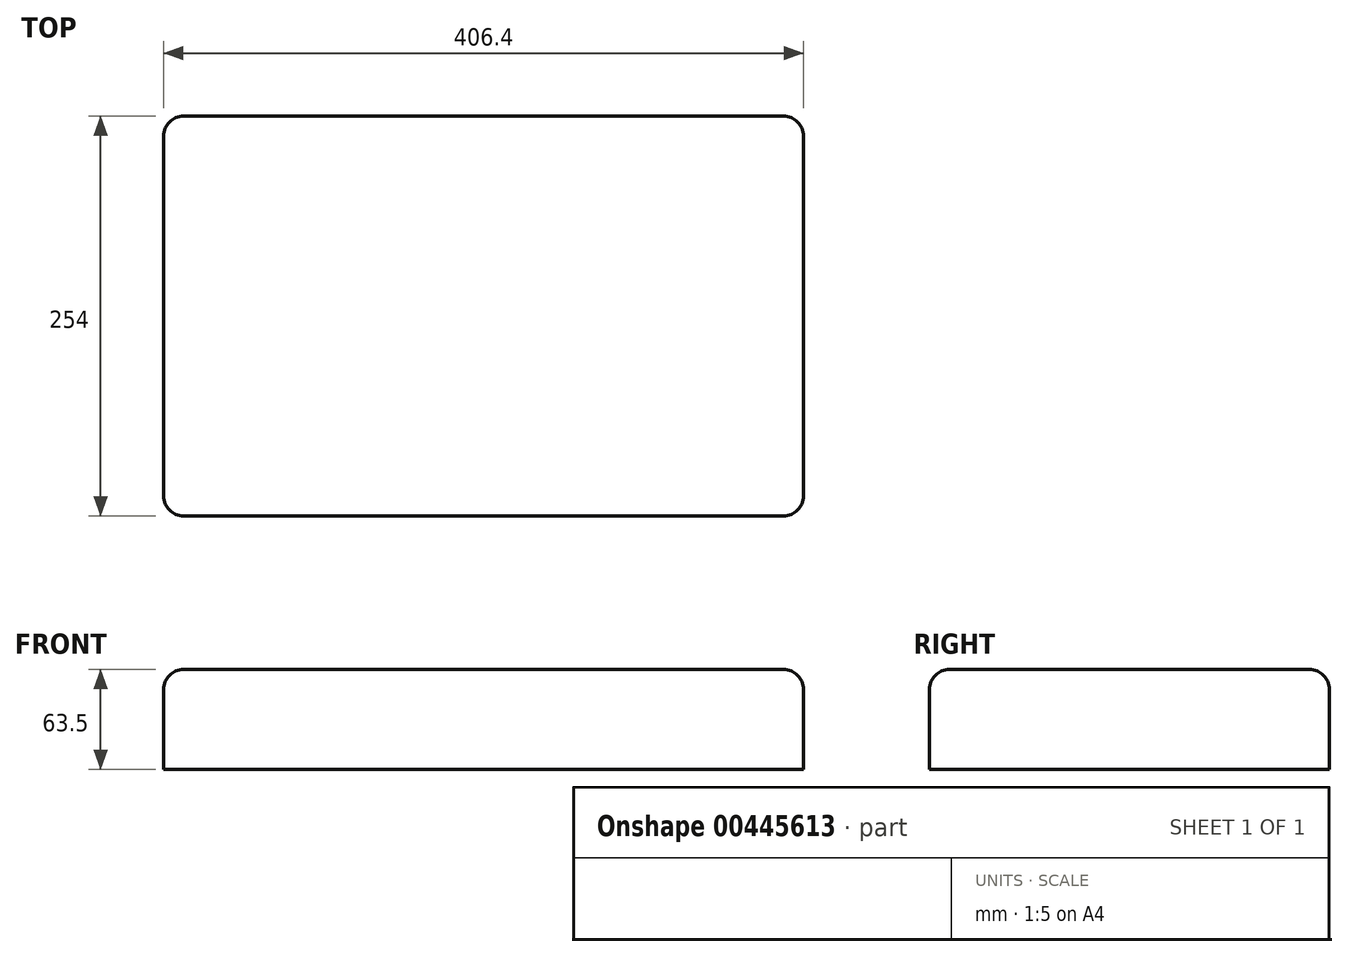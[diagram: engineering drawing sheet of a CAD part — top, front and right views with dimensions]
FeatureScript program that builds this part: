
annotation { "Feature Type Name" : "Feature", "Feature Type Description" : "" }
export const myFeature = defineFeature(function(context is Context, id is Id, definition is map)
    precondition{}
    {
        {
            var Q0;
            Q0=qCreatedBy(makeId("Top.planeOp"),FACE);
            var sketch = newSketch(context, id + "F0", { "sketchPlane" : qUnion([Q0])});
            skLineSegment(sketch, "E0.bottom", {"start": v(203.2, 127) * mm, "end": v(-203.2, 127) * mm});
            skLineSegment(sketch, "E0.top", {"start": v(203.2, -127) * mm, "end": v(-203.2, -127) * mm});
            skLineSegment(sketch, "E0.left", {"start": v(203.2, 127) * mm, "end": v(203.2, -127) * mm});
            skLineSegment(sketch, "E0.right", {"start": v(-203.2, 127) * mm, "end": v(-203.2, -127) * mm});
            skPoint(sketch, "E0.middle", {"position": v(0, 0) * mm});
            skSolve(sketch);
        }
        {
            var Q0;
            Q0 = qSketchRegion(id + "F0", true);
            extrude(context, id + "F1", {"entities" : qUnion([Q0]), "depth" : 63.5 * mm});
        }
        {
            var Q0;
            Q0=makeQuery(id+"F1.opExtrude","SWEPT_EDGE",EDGE,{"disambiguationData":[OSD([sQuery(id+"F0.wireOp",EDGE,"E0.top"),sQuery(id+"F0.wireOp",EDGE,"E0.left")])]});
            fillet(context, id + "F2", {"entities" : qUnion([Q0]), "radius" : 12.7 * mm, "tangentPropagation" : true, "allowEdgeOverflow" : false});
        }
        {
            var Q0;
            Q0=makeQuery(id+"F1.opExtrude","CAP_EDGE",EDGE,{"disambiguationData":[OSD([sQuery(id+"F0.wireOp",EDGE,"E0.top")])],"isStart":false});
            fillet(context, id + "F3", {"entities" : qUnion([Q0]), "radius" : 12.7 * mm, "tangentPropagation" : true, "allowEdgeOverflow" : false});
        }
        {
            var Q0;
            Q0=makeQuery(id+"F1.opExtrude","SWEPT_EDGE",EDGE,{"disambiguationData":[OSD([sQuery(id+"F0.wireOp",EDGE,"E0.bottom"),sQuery(id+"F0.wireOp",EDGE,"E0.left")])]});
            fillet(context, id + "F4", {"entities" : qUnion([Q0]), "radius" : 12.7 * mm, "tangentPropagation" : true, "allowEdgeOverflow" : false});
        }
        {
            var Q0;
            Q0=makeQuery(id+"F1.opExtrude","CAP_EDGE",EDGE,{"disambiguationData":[OSD([sQuery(id+"F0.wireOp",EDGE,"E0.right")])],"isStart":false});
            fillet(context, id + "F5", {"entities" : qUnion([Q0]), "radius" : 12.7 * mm, "tangentPropagation" : true, "allowEdgeOverflow" : false});
        }
    });
